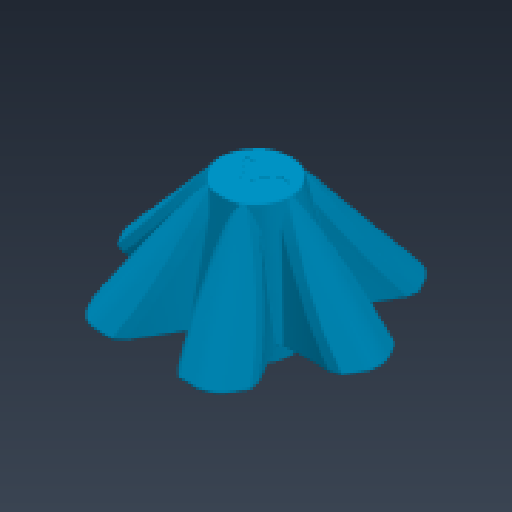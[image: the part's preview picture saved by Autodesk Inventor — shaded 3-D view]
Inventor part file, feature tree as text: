
AUTODESK INVENTOR PART (.ipt)
format: ipt  version: 2024.3 (Build 283343000, 343)  size: 4,642,816 bytes
history: native  units: in
note: dims shown in document units (in); Inventor stores cm internally (conversion verified against a paired STEP export)
features: fillet x1
ambient origin geometry x8: Origin, YZ Plane, XZ Plane, XY Plane, X Axis, Y Axis, Z Axis, Center Point
bodies: Solid1 (feature_tree)
feature tree (1):
  fillet  "Fillet156"  [1 undecoded]
note: 1 required parameter value undecoded (feature->parameter linkage not recoverable at this tier; creation-order binding heuristic only, values carry confidence <= 0.55)
